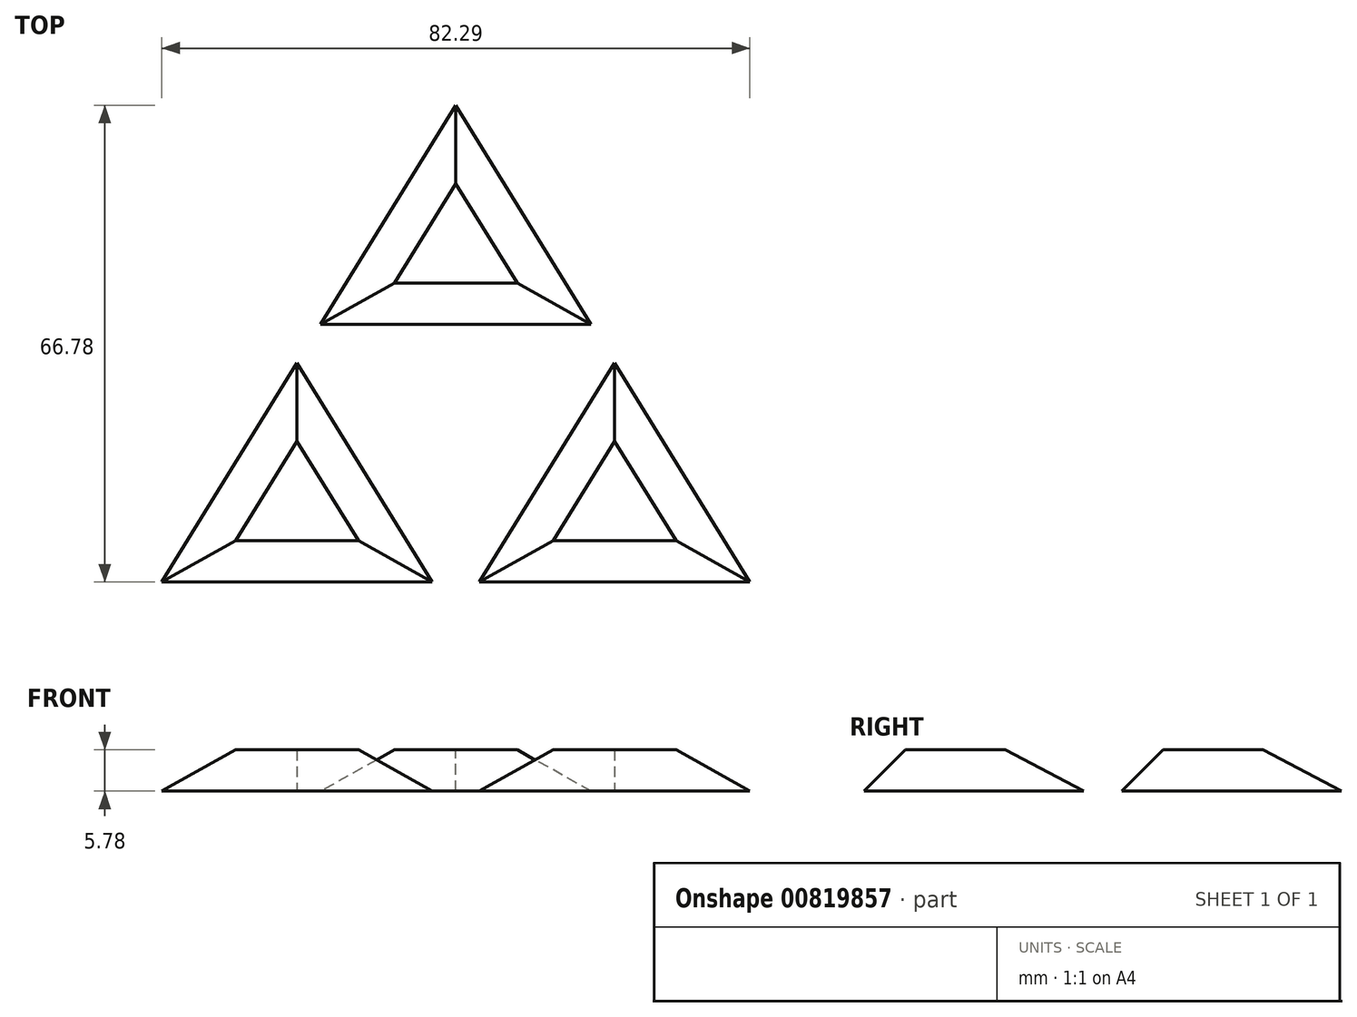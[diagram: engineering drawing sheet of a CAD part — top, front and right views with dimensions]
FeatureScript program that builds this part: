
annotation { "Feature Type Name" : "Feature", "Feature Type Description" : "" }
export const myFeature = defineFeature(function(context is Context, id is Id, definition is map)
    precondition{}
    {
        {
            var Q0;
            Q0=qCreatedBy(makeId("Top.planeOp"),FACE);
            var sketch = newSketch(context, id + "F0", { "sketchPlane" : qUnion([Q0])});
            skLineSegment(sketch, "E0", {"start": v(-44.99, -11.26) * mm, "end": v(43.91, -11.26) * mm});
            skLineSegment(sketch, "E1", {"start": v(-44.99, -11.26) * mm, "end": v(-0.54, 60.87) * mm});
            skPoint(sketch, "E1.endSnap0", {"position": v(-0.54, -11.26) * mm});
            skLineSegment(sketch, "E2", {"start": v(-0.54, 60.87) * mm, "end": v(43.91, -11.26) * mm});
            skLineSegment(sketch, "E3", {"start": v(-0.54, -11.26) * mm, "end": v(-22.76, 24.8) * mm});
            skLineSegment(sketch, "E4", {"start": v(-22.76, 24.8) * mm, "end": v(21.69, 24.8) * mm});
            skLineSegment(sketch, "E5", {"start": v(21.69, 24.8) * mm, "end": v(-0.54, -11.26) * mm});
            skSolve(sketch);
        }
        {
            var Q0;
            {var subQ3=sQuery(id+"F0.wireOp",EDGE,"E5");Q0=makeQuery(id+"F0.imprint","IMPRINT",FACE,{"disambiguationData":[TD([[makeQuery(id+"F0.imprint","IMPRINT",EDGE,{"derivedFrom":subQ3}),1.0]])]});}
            var Q1;
            {var subQ3=sQuery(id+"F0.wireOp",EDGE,"E3");Q1=makeQuery(id+"F0.imprint","IMPRINT",FACE,{"disambiguationData":[TD([[makeQuery(id+"F0.imprint","IMPRINT",EDGE,{"derivedFrom":subQ3}),1.0]])]});}
            var Q2;
            {var subQ3=sQuery(id+"F0.wireOp",EDGE,"E4");Q2=makeQuery(id+"F0.imprint","IMPRINT",FACE,{"disambiguationData":[TD([[makeQuery(id+"F0.imprint","IMPRINT",EDGE,{"derivedFrom":subQ3}),1.0]])]});}
            extrude(context, id + "F1", {"entities" : qUnion([Q0, Q1, Q2]), "depth" : 5.78 * mm, "offsetDistance" : 25.4 * mm});
        }
        {
            var Q0;
            {var subQ0=sQuery(id+"F0.wireOp",EDGE,"E0");Q0=makeQuery(id+"F1.opExtrude","CAP_EDGE",EDGE,{"disambiguationData":[OSD([subQ0]),TDD([makeQuery(id+"F0.imprint","IMPRINT",EDGE,{"disambiguationData":[TD([[makeQuery(id+"F0.imprint","INTERSECT",VERTEX,{"derivedFrom":[subQ0,sQuery(id+"F0.wireOp",EDGE,"E2")]}),1.0]])],"derivedFrom":subQ0})])],"isStart":false});}
            var Q1;
            {var subQ0=sQuery(id+"F0.wireOp",EDGE,"E2");Q1=makeQuery(id+"F1.opExtrude","CAP_EDGE",EDGE,{"disambiguationData":[OSD([subQ0]),TDD([makeQuery(id+"F0.imprint","IMPRINT",EDGE,{"disambiguationData":[TD([[makeQuery(id+"F0.imprint","INTERSECT",VERTEX,{"derivedFrom":[sQuery(id+"F0.wireOp",EDGE,"E0"),subQ0]}),1.0]])],"derivedFrom":subQ0})])],"isStart":false});}
            var Q2;
            Q2=makeQuery(id+"F1.opExtrude","CAP_EDGE",EDGE,{"disambiguationData":[OSD([sQuery(id+"F0.wireOp",EDGE,"E5")])],"isStart":false});
            var Q3;
            {var subQ0=sQuery(id+"F0.wireOp",EDGE,"E0");Q3=makeQuery(id+"F1.opExtrude","CAP_EDGE",EDGE,{"disambiguationData":[OSD([subQ0]),TDD([makeQuery(id+"F0.imprint","IMPRINT",EDGE,{"disambiguationData":[TD([[makeQuery(id+"F0.imprint","INTERSECT",VERTEX,{"derivedFrom":[subQ0,sQuery(id+"F0.wireOp",EDGE,"E1")]}),-1.0]])],"derivedFrom":subQ0})])],"isStart":false});}
            var Q4;
            Q4=makeQuery(id+"F1.opExtrude","CAP_EDGE",EDGE,{"disambiguationData":[OSD([sQuery(id+"F0.wireOp",EDGE,"E3")])],"isStart":false});
            var Q5;
            {var subQ0=sQuery(id+"F0.wireOp",EDGE,"E1");Q5=makeQuery(id+"F1.opExtrude","CAP_EDGE",EDGE,{"disambiguationData":[OSD([subQ0]),TDD([makeQuery(id+"F0.imprint","IMPRINT",EDGE,{"disambiguationData":[TD([[makeQuery(id+"F0.imprint","INTERSECT",VERTEX,{"derivedFrom":[sQuery(id+"F0.wireOp",EDGE,"E0"),subQ0]}),-1.0]])],"derivedFrom":subQ0})])],"isStart":false});}
            var Q6;
            {var subQ0=sQuery(id+"F0.wireOp",EDGE,"E1");Q6=makeQuery(id+"F1.opExtrude","CAP_EDGE",EDGE,{"disambiguationData":[OSD([subQ0]),TDD([makeQuery(id+"F0.imprint","IMPRINT",EDGE,{"disambiguationData":[TD([[makeQuery(id+"F0.imprint","INTERSECT",VERTEX,{"derivedFrom":[subQ0,sQuery(id+"F0.wireOp",EDGE,"E2")]}),1.0]])],"derivedFrom":subQ0})])],"isStart":false});}
            var Q7;
            Q7=makeQuery(id+"F1.opExtrude","CAP_EDGE",EDGE,{"disambiguationData":[OSD([sQuery(id+"F0.wireOp",EDGE,"E4")])],"isStart":false});
            var Q8;
            {var subQ0=sQuery(id+"F0.wireOp",EDGE,"E2");Q8=makeQuery(id+"F1.opExtrude","CAP_EDGE",EDGE,{"disambiguationData":[OSD([subQ0]),TDD([makeQuery(id+"F0.imprint","IMPRINT",EDGE,{"disambiguationData":[TD([[makeQuery(id+"F0.imprint","INTERSECT",VERTEX,{"derivedFrom":[sQuery(id+"F0.wireOp",EDGE,"E1"),subQ0]}),-1.0]])],"derivedFrom":subQ0})])],"isStart":false});}
            chamfer(context, id + "F2", {"entities" : qUnion([Q0, Q1, Q2, Q3, Q4, Q5, Q6, Q7, Q8]), "width" : 7.62 * mm, "tangentPropagation" : true});
        }
    });
